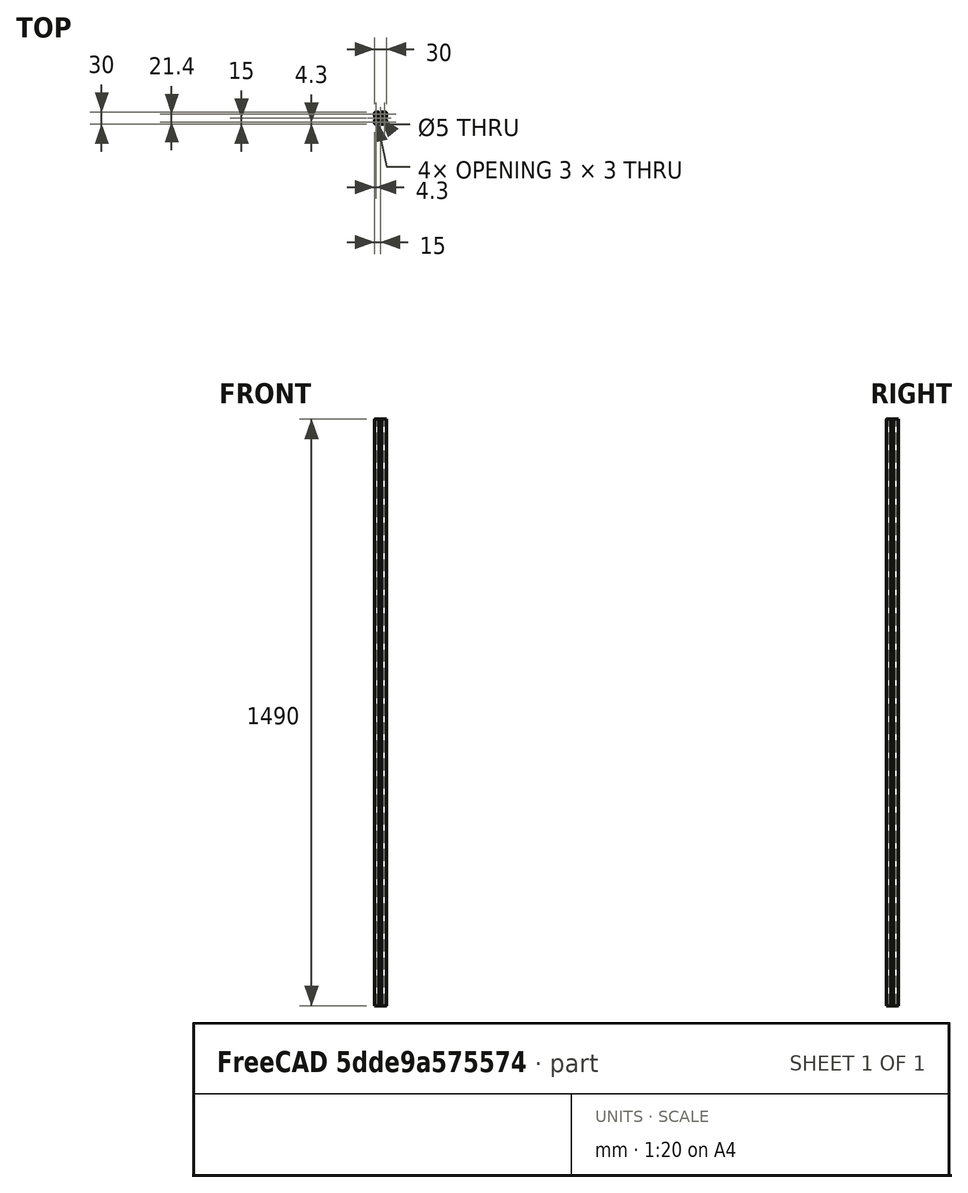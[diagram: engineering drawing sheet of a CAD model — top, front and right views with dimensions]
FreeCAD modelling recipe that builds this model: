
FCSTD DOCUMENT  (FreeCAD 0.19R18353 (Git))
Label: Profile_3030-1490
License: CreativeCommons Attribution
LicenseURL: http://creativecommons.org/licenses/by/4.0/
objects: Sketcher::SketchObject×1, PartDesign::Pad×1, PartDesign::Body×1
note: 4 computed .brp shape members not serialized (recipe doc carries the construction recipe); baked Part::Feature solids carry a one-line shape summary decoded from their .brp

FEATURE [Sketcher::SketchObject] Sketch
  MapMode = 5
  Support = -> [XY_Plane]
  sketch-geometry (137):
    g0: LineSegment [constr] StartX=-5.2 StartY=5.2 StartZ=0 EndX=5.2 EndY=5.2 EndZ=0
    g1: LineSegment [constr] StartX=5.2 StartY=5.2 StartZ=0 EndX=5.2 EndY=-5.2 EndZ=0
    g2: LineSegment [constr] StartX=5.2 StartY=-5.2 StartZ=0 EndX=-5.2 EndY=-5.2 EndZ=0
    g3: LineSegment [constr] StartX=-5.2 StartY=-5.2 StartZ=0 EndX=-5.2 EndY=5.2 EndZ=0
    g4: LineSegment [constr] StartX=-15 StartY=15 StartZ=0 EndX=15 EndY=15 EndZ=0
    g5: LineSegment [constr] StartX=15 StartY=15 StartZ=0 EndX=15 EndY=-15 EndZ=0
    g6: LineSegment [constr] StartX=15 StartY=-15 StartZ=0 EndX=-15 EndY=-15 EndZ=0
    g7: LineSegment [constr] StartX=-15 StartY=-15 StartZ=0 EndX=-15 EndY=15 EndZ=0
    g8: LineSegment [constr] StartX=-12.2 StartY=12.2 StartZ=0 EndX=12.2 EndY=12.2 EndZ=0
    g9: LineSegment [constr] StartX=12.2 StartY=12.2 StartZ=0 EndX=12.2 EndY=-12.2 EndZ=0
    g10: LineSegment [constr] StartX=12.2 StartY=-12.2 StartZ=0 EndX=-12.2 EndY=-12.2 EndZ=0
    g11: LineSegment [constr] StartX=-12.2 StartY=-12.2 StartZ=0 EndX=-12.2 EndY=12.2 EndZ=0
    g12: Circle CenterX=0 CenterY=0 CenterZ=0 NormalX=0 NormalY=0 NormalZ=1 AngleXU=0 Radius=2.5
    g13: LineSegment [constr] StartX=15 StartY=15 StartZ=0 EndX=5.2 EndY=5.2 EndZ=0
    g14: LineSegment [constr] StartX=13.5151 StartY=15 StartZ=0 EndX=15 EndY=13.5151 EndZ=0
    g15: LineSegment [constr] StartX=15 StartY=13.5151 StartZ=0 EndX=5.2 EndY=3.71508 EndZ=0
    g16: LineSegment [constr] StartX=5.2 StartY=3.71508 StartZ=0 EndX=3.71508 EndY=5.2 EndZ=0
    g17: LineSegment [constr] StartX=3.71508 StartY=5.2 StartZ=0 EndX=13.5151 EndY=15 EndZ=0
    g18: LineSegment [constr] StartX=5.2 StartY=-5.2 StartZ=0 EndX=15 EndY=-15 EndZ=0
    g19: LineSegment [constr] StartX=-8.15 StartY=8.15 StartZ=0 EndX=8.15 EndY=8.15 EndZ=0
    g20: LineSegment [constr] StartX=8.15 StartY=8.15 StartZ=0 EndX=8.15 EndY=-8.15 EndZ=0
    g21: LineSegment [constr] StartX=8.15 StartY=-8.15 StartZ=0 EndX=-8.15 EndY=-8.15 EndZ=0
    g22: LineSegment [constr] StartX=-8.15 StartY=-8.15 StartZ=0 EndX=-8.15 EndY=8.15 EndZ=0
    g23: LineSegment [constr] StartX=-15 StartY=3.15 StartZ=0 EndX=15 EndY=3.15 EndZ=0
    g24: LineSegment [constr] StartX=15 StartY=3.15 StartZ=0 EndX=15 EndY=-3.15 EndZ=0
    g25: LineSegment [constr] StartX=15 StartY=-3.15 StartZ=0 EndX=-15 EndY=-3.15 EndZ=0
    g26: LineSegment [constr] StartX=-15 StartY=-3.15 StartZ=0 EndX=-15 EndY=3.15 EndZ=0
    g27: LineSegment [constr] StartX=5.2 StartY=-3.71508 StartZ=0 EndX=3.71508 EndY=-5.2 EndZ=0
    g28: LineSegment [constr] StartX=3.71508 StartY=-5.2 StartZ=0 EndX=13.5151 EndY=-15 EndZ=0
    g29: LineSegment [constr] StartX=13.5151 StartY=-15 StartZ=0 EndX=15 EndY=-13.5151 EndZ=0
    g30: LineSegment [constr] StartX=15 StartY=-13.5151 StartZ=0 EndX=5.2 EndY=-3.71508 EndZ=0
    g31: LineSegment StartX=14 StartY=3.15 StartZ=0 EndX=12.2 EndY=3.15 EndZ=0
    g32: LineSegment StartX=12.2 StartY=3.15 StartZ=0 EndX=12.2 EndY=8.15 EndZ=0
    g33: LineSegment StartX=12.2 StartY=8.15 StartZ=0 EndX=9.63492 EndY=8.15 EndZ=0
    g34: LineSegment StartX=9.63492 StartY=8.15 StartZ=0 EndX=5.2 EndY=3.71508 EndZ=0
    g35: LineSegment StartX=5.2 StartY=3.71508 StartZ=0 EndX=5.2 EndY=-3.71508 EndZ=0
    g36: LineSegment StartX=5.2 StartY=-3.71508 StartZ=0 EndX=9.63492 EndY=-8.15 EndZ=0
    g37: LineSegment StartX=9.63492 StartY=-8.15 StartZ=0 EndX=12.2 EndY=-8.15 EndZ=0
    g38: LineSegment StartX=12.2 StartY=-8.15 StartZ=0 EndX=12.2 EndY=-3.15 EndZ=0
    g39: LineSegment StartX=12.2 StartY=-3.15 StartZ=0 EndX=14 EndY=-3.15 EndZ=0
    g40: LineSegment [constr] StartX=-3.15 StartY=15 StartZ=0 EndX=3.15 EndY=15 EndZ=0
    g41: LineSegment [constr] StartX=3.15 StartY=15 StartZ=0 EndX=3.15 EndY=-15 EndZ=0
    g42: LineSegment [constr] StartX=3.15 StartY=-15 StartZ=0 EndX=-3.15 EndY=-15 EndZ=0
    g43: LineSegment [constr] StartX=-3.15 StartY=-15 StartZ=0 EndX=-3.15 EndY=15 EndZ=0
    g44: LineSegment [constr] StartX=-15 StartY=15 StartZ=0 EndX=-5.2 EndY=5.2 EndZ=0
    g45: LineSegment [constr] StartX=-5.2 StartY=-5.2 StartZ=0 EndX=-15 EndY=-15 EndZ=0
    g46: LineSegment [constr] StartX=-13.5151 StartY=15 StartZ=0 EndX=-15 EndY=13.5151 EndZ=0
    g47: LineSegment [constr] StartX=-15 StartY=13.5151 StartZ=0 EndX=-5.2 EndY=3.71508 EndZ=0
    g48: LineSegment [constr] StartX=-5.2 StartY=3.71508 StartZ=0 EndX=-3.71508 EndY=5.2 EndZ=0
    g49: LineSegment [constr] StartX=-3.71508 StartY=5.2 StartZ=0 EndX=-13.5151 EndY=15 EndZ=0
    g50: LineSegment StartX=15 StartY=4.15 StartZ=0 EndX=15 EndY=13 EndZ=0
    g51: LineSegment StartX=13 StartY=15 StartZ=0 EndX=4.15 EndY=15 EndZ=0
    g52: LineSegment StartX=3.15 StartY=14 StartZ=0 EndX=3.15 EndY=12.2 EndZ=0
    g53: LineSegment StartX=3.15 StartY=12.2 StartZ=0 EndX=8.15 EndY=12.2 EndZ=0
    g54: LineSegment StartX=8.15 StartY=12.2 StartZ=0 EndX=8.15 EndY=9.63492 EndZ=0
    g55: LineSegment StartX=8.15 StartY=9.63492 StartZ=0 EndX=3.71508 EndY=5.2 EndZ=0
    g56: LineSegment StartX=3.71508 StartY=5.2 StartZ=0 EndX=-3.71508 EndY=5.2 EndZ=0
    g57: LineSegment StartX=-3.71508 StartY=5.2 StartZ=0 EndX=-8.15 EndY=9.63492 EndZ=0
    g58: LineSegment StartX=-8.15 StartY=9.63492 StartZ=0 EndX=-8.15 EndY=12.2 EndZ=0
    g59: LineSegment StartX=-8.15 StartY=12.2 StartZ=0 EndX=-3.15 EndY=12.2 EndZ=0
    g60: LineSegment StartX=-3.15 StartY=12.2 StartZ=0 EndX=-3.15 EndY=14 EndZ=0
    g61: LineSegment StartX=-4.15 StartY=15 StartZ=0 EndX=-13 EndY=15 EndZ=0
    g62: ArcOfCircle CenterX=13 CenterY=13 CenterZ=0 NormalX=0 NormalY=0 NormalZ=1 AngleXU=0 Radius=2 StartAngle=0 EndAngle=1.5708
    g63: LineSegment [constr] StartX=-15 StartY=-13.5151 StartZ=0 EndX=-13.5151 EndY=-15 EndZ=0
    g64: LineSegment [constr] StartX=-13.5151 StartY=-15 StartZ=0 EndX=-3.71508 EndY=-5.2 EndZ=0
    g65: LineSegment [constr] StartX=-3.71508 StartY=-5.2 StartZ=0 EndX=-5.2 EndY=-3.71508 EndZ=0
    g66: LineSegment [constr] StartX=-5.2 StartY=-3.71508 StartZ=0 EndX=-15 EndY=-13.5151 EndZ=0
    g67: LineSegment StartX=-15 StartY=13 StartZ=0 EndX=-15 EndY=4.15 EndZ=0
    g68: LineSegment StartX=-14 StartY=3.15 StartZ=0 EndX=-12.2 EndY=3.15 EndZ=0
    g69: LineSegment StartX=-12.2 StartY=3.15 StartZ=0 EndX=-12.2 EndY=8.15 EndZ=0
    g70: LineSegment StartX=-9.63492 StartY=8.15 StartZ=0 EndX=-5.2 EndY=3.71508 EndZ=0
    g71: LineSegment StartX=-5.2 StartY=3.71508 StartZ=0 EndX=-5.2 EndY=-3.71508 EndZ=0
    g72: LineSegment StartX=-5.2 StartY=-3.71508 StartZ=0 EndX=-9.63492 EndY=-8.15 EndZ=0
    g73: LineSegment StartX=-12.2 StartY=-8.15 StartZ=0 EndX=-12.2 EndY=-3.15 EndZ=0
    g74: LineSegment StartX=-12.2 StartY=-3.15 StartZ=0 EndX=-14 EndY=-3.15 EndZ=0
    g75: LineSegment StartX=-15 StartY=-4.15 StartZ=0 EndX=-15 EndY=-13 EndZ=0
    g76: ArcOfCircle CenterX=14 CenterY=4.15 CenterZ=0 NormalX=0 NormalY=0 NormalZ=1 AngleXU=0 Radius=1 StartAngle=4.71239 EndAngle=6.28319
    g77: ArcOfCircle CenterX=4.15 CenterY=14 CenterZ=0 NormalX=0 NormalY=0 NormalZ=1 AngleXU=0 Radius=1 StartAngle=1.5708 EndAngle=3.14159
    g78: ArcOfCircle CenterX=-4.15 CenterY=14 CenterZ=0 NormalX=0 NormalY=0 NormalZ=1 AngleXU=0 Radius=1 StartAngle=0 EndAngle=1.5708
    g79: ArcOfCircle CenterX=-13 CenterY=13 CenterZ=0 NormalX=0 NormalY=0 NormalZ=1 AngleXU=0 Radius=2 StartAngle=1.5708 EndAngle=3.14159
    g80: ArcOfCircle CenterX=-14 CenterY=4.15 CenterZ=0 NormalX=0 NormalY=0 NormalZ=1 AngleXU=0 Radius=1 StartAngle=3.14159 EndAngle=4.71239
    g81: ArcOfCircle CenterX=-14 CenterY=-4.15 CenterZ=0 NormalX=0 NormalY=0 NormalZ=1 AngleXU=0 Radius=1 StartAngle=1.5708 EndAngle=3.14159
    g82: LineSegment StartX=15 StartY=-4.15 StartZ=0 EndX=15 EndY=-13 EndZ=0
    g83: LineSegment StartX=13 StartY=-15 StartZ=0 EndX=4.15 EndY=-15 EndZ=0
    g84: LineSegment StartX=3.15 StartY=-14 StartZ=0 EndX=3.15 EndY=-12.2 EndZ=0
    g85: LineSegment StartX=3.15 StartY=-12.2 StartZ=0 EndX=8.15 EndY=-12.2 EndZ=0
    g86: LineSegment StartX=8.15 StartY=-12.2 StartZ=0 EndX=8.15 EndY=-9.63492 EndZ=0
    g87: LineSegment StartX=8.15 StartY=-9.63492 StartZ=0 EndX=3.71508 EndY=-5.2 EndZ=0
    g88: LineSegment StartX=3.71508 StartY=-5.2 StartZ=0 EndX=-3.71508 EndY=-5.2 EndZ=0
    g89: LineSegment StartX=-3.71508 StartY=-5.2 StartZ=0 EndX=-8.15 EndY=-9.63492 EndZ=0
    g90: LineSegment StartX=-8.15 StartY=-9.63492 StartZ=0 EndX=-8.15 EndY=-12.2 EndZ=0
    g91: LineSegment StartX=-8.15 StartY=-12.2 StartZ=0 EndX=-3.15 EndY=-12.2 EndZ=0
    g92: LineSegment StartX=-3.15 StartY=-12.2 StartZ=0 EndX=-3.15 EndY=-14 EndZ=0
    g93: LineSegment StartX=-4.15 StartY=-15 StartZ=0 EndX=-13 EndY=-15 EndZ=0
    g94: ArcOfCircle CenterX=4.15 CenterY=-14 CenterZ=0 NormalX=0 NormalY=0 NormalZ=1 AngleXU=0 Radius=1 StartAngle=3.14159 EndAngle=4.71239
    g95: ArcOfCircle CenterX=-4.15 CenterY=-14 CenterZ=0 NormalX=0 NormalY=0 NormalZ=1 AngleXU=0 Radius=1 StartAngle=4.71239 EndAngle=6.28319
    g96: ArcOfCircle CenterX=-13 CenterY=-13 CenterZ=0 NormalX=0 NormalY=0 NormalZ=1 AngleXU=0 Radius=2 StartAngle=3.14159 EndAngle=4.71239
    g97: ArcOfCircle CenterX=13 CenterY=-13 CenterZ=0 NormalX=0 NormalY=0 NormalZ=1 AngleXU=0 Radius=2 StartAngle=4.71239 EndAngle=6.28319
    g98: ArcOfCircle CenterX=14 CenterY=-4.15 CenterZ=0 NormalX=0 NormalY=0 NormalZ=1 AngleXU=0 Radius=1 StartAngle=0 EndAngle=1.5708
    g99: LineSegment StartX=-12.2 StartY=8.15 StartZ=0 EndX=-9.63492 EndY=8.15 EndZ=0
    g100: LineSegment StartX=-12.2 StartY=-8.15 StartZ=0 EndX=-9.63492 EndY=-8.15 EndZ=0
    g101: LineSegment [constr] StartX=9.2 StartY=12.2 StartZ=0 EndX=12.2 EndY=12.2 EndZ=0
    g102: LineSegment [constr] StartX=12.2 StartY=12.2 StartZ=0 EndX=12.2 EndY=9.2 EndZ=0
    g103: LineSegment [constr] StartX=12.2 StartY=9.2 StartZ=0 EndX=9.2 EndY=9.2 EndZ=0
    g104: LineSegment [constr] StartX=9.2 StartY=9.2 StartZ=0 EndX=9.2 EndY=12.2 EndZ=0
    g105: LineSegment StartX=9.2 StartY=12.2 StartZ=0 EndX=11.2 EndY=12.2 EndZ=0
    g106: LineSegment StartX=12.2 StartY=9.2 StartZ=0 EndX=9.2 EndY=9.2 EndZ=0
    g107: LineSegment StartX=9.2 StartY=9.2 StartZ=0 EndX=9.2 EndY=12.2 EndZ=0
    g108: ArcOfCircle CenterX=11.2 CenterY=11.2 CenterZ=0 NormalX=0 NormalY=0 NormalZ=1 AngleXU=0 Radius=1 StartAngle=6e-16 EndAngle=1.5708
    g109: LineSegment StartX=12.2 StartY=11.2 StartZ=0 EndX=12.2 EndY=9.2 EndZ=0
    g110: LineSegment [constr] StartX=-12.2 StartY=12.2 StartZ=0 EndX=-9.2 EndY=12.2 EndZ=0
    g111: LineSegment [constr] StartX=-9.2 StartY=12.2 StartZ=0 EndX=-9.2 EndY=9.2 EndZ=0
    g112: LineSegment [constr] StartX=-9.2 StartY=9.2 StartZ=0 EndX=-12.2 EndY=9.2 EndZ=0
    g113: LineSegment [constr] StartX=-12.2 StartY=9.2 StartZ=0 EndX=-12.2 EndY=12.2 EndZ=0
    g114: ArcOfCircle CenterX=-11.2 CenterY=11.2 CenterZ=0 NormalX=0 NormalY=0 NormalZ=1 AngleXU=0 Radius=1 StartAngle=1.5708 EndAngle=3.14159
    g115: LineSegment StartX=-11.2 StartY=12.2 StartZ=0 EndX=-9.2 EndY=12.2 EndZ=0
    g116: LineSegment StartX=-9.2 StartY=12.2 StartZ=0 EndX=-9.2 EndY=9.2 EndZ=0
    g117: LineSegment StartX=-9.2 StartY=9.2 StartZ=0 EndX=-12.2 EndY=9.2 EndZ=0
    g118: LineSegment StartX=-12.2 StartY=9.2 StartZ=0 EndX=-12.2 EndY=11.2 EndZ=0
    g119: LineSegment [constr] StartX=-12.2 StartY=-9.2 StartZ=0 EndX=-9.2 EndY=-9.2 EndZ=0
    g120: LineSegment [constr] StartX=-9.2 StartY=-9.2 StartZ=0 EndX=-9.2 EndY=-12.2 EndZ=0
    g121: LineSegment [constr] StartX=-9.2 StartY=-12.2 StartZ=0 EndX=-12.2 EndY=-12.2 EndZ=0
    g122: LineSegment [constr] StartX=-12.2 StartY=-12.2 StartZ=0 EndX=-12.2 EndY=-9.2 EndZ=0
    g123: ArcOfCircle CenterX=-11.2 CenterY=-11.2 CenterZ=0 NormalX=0 NormalY=0 NormalZ=1 AngleXU=0 Radius=1 StartAngle=3.14159 EndAngle=4.71239
    g124: LineSegment StartX=-12.2 StartY=-11.2 StartZ=0 EndX=-12.2 EndY=-9.2 EndZ=0
    g125: LineSegment StartX=-12.2 StartY=-9.2 StartZ=0 EndX=-9.2 EndY=-9.2 EndZ=0
    g126: LineSegment StartX=-9.2 StartY=-9.2 StartZ=0 EndX=-9.2 EndY=-12.2 EndZ=0
    g127: LineSegment StartX=-9.2 StartY=-12.2 StartZ=0 EndX=-11.2 EndY=-12.2 EndZ=0
    g128: LineSegment [constr] StartX=9.2 StartY=-9.2 StartZ=0 EndX=12.2 EndY=-9.2 EndZ=0
    g129: LineSegment [constr] StartX=12.2 StartY=-9.2 StartZ=0 EndX=12.2 EndY=-12.2 EndZ=0
    g130: LineSegment [constr] StartX=12.2 StartY=-12.2 StartZ=0 EndX=9.2 EndY=-12.2 EndZ=0
    g131: LineSegment [constr] StartX=9.2 StartY=-12.2 StartZ=0 EndX=9.2 EndY=-9.2 EndZ=0
    g132: ArcOfCircle CenterX=11.2 CenterY=-11.2 CenterZ=0 NormalX=0 NormalY=0 NormalZ=1 AngleXU=0 Radius=1 StartAngle=4.71239 EndAngle=6.28319
    g133: LineSegment StartX=12.2 StartY=-11.2 StartZ=0 EndX=12.2 EndY=-9.2 EndZ=0
    g134: LineSegment StartX=12.2 StartY=-9.2 StartZ=0 EndX=9.2 EndY=-9.2 EndZ=0
    g135: LineSegment StartX=9.2 StartY=-9.2 StartZ=0 EndX=9.2 EndY=-12.2 EndZ=0
    g136: LineSegment StartX=9.2 StartY=-12.2 StartZ=0 EndX=11.2 EndY=-12.2 EndZ=0
  constraints (360):
    c: Coincident(g0,g1)
    c: Coincident(g1,g2)
    c: Coincident(g2,g3)
    c: Coincident(g3,g0)
    c: Horizontal(g0)
    c: Horizontal(g2)
    c: Vertical(g1)
    c: Vertical(g3)
    c: Coincident(g4,g5)
    c: Coincident(g5,g6)
    c: Coincident(g6,g7)
    c: Coincident(g7,g4)
    c: Horizontal(g4)
    c: Horizontal(g6)
    c: Vertical(g5)
    c: Vertical(g7)
    c: Coincident(g8,g9)
    c: Coincident(g9,g10)
    c: Coincident(g10,g11)
    c: Coincident(g11,g8)
    c: Horizontal(g8)
    c: Horizontal(g10)
    c: Vertical(g9)
    c: Vertical(g11)
    c: Symmetric(g1,g0,g-1)
    c: Equal(g0,g1)
    c: Symmetric(g8,g9,g-1)
    c: Equal(g8,g9)
    c: Symmetric(g4,g5,g-1)
    c: Equal(g4,g5)
    c: Diameter(g12) = 5
    c: Coincident(g12,g-1)
    c: DistanceY(g1,g1) = 10.4
    c: DistanceY(g5,g5) = 30
    c: DistanceY(g8,g4) = 2.8
    c: Coincident(g13,g4)
    c: Coincident(g13,g0)
    c: Coincident(g14,g15)
    c: Coincident(g15,g16)
    c: Coincident(g16,g17)
    c: Coincident(g17,g14)
    c: Parallel(g17,g13)
    c: Parallel(g13,g15)
    c: Angle(g17,g14) = 1.5708
    c: Angle(g16,g17) = 1.5708
    c: PointOnObject(g15,g1)
    c: PointOnObject(g16,g0)
    c: Distance(g15,g16) = 2.1
    c: PointOnObject(g14,g5)
    c: Coincident(g18,g1)
    c: Coincident(g18,g5)
    c: Coincident(g19,g20)
    c: Coincident(g20,g21)
    c: Coincident(g21,g22)
    c: Coincident(g22,g19)
    c: Horizontal(g19)
    c: Horizontal(g21)
    c: Vertical(g20)
    c: Vertical(g22)
    c: Symmetric(g20,g19,g-1)
    c: Equal(g19,g20)
    c: DistanceY(g20,g20) = 16.3
    c: Coincident(g23,g24)
    c: Coincident(g24,g25)
    c: Coincident(g25,g26)
    c: Coincident(g26,g23)
    c: Horizontal(g23)
    c: Horizontal(g25)
    c: Vertical(g24)
    c: Vertical(g26)
    c: Symmetric(g24,g23,g-1)
    c: DistanceY(g25,g23) = 6.3
    c: PointOnObject(g25,g7)
    c: Coincident(g27,g28)
    c: Coincident(g28,g29)
    c: Coincident(g29,g30)
    c: Coincident(g30,g27)
    c: Equal(g28,g18)
    c: Equal(g18,g30)
    c: PointOnObject(g27,g1)
    c: PointOnObject(g27,g2)
    c: PointOnObject(g28,g6)
    c: PointOnObject(g29,g5)
    c: Angle(g30,g29) = 1.5708
    c: Distance(g29,g28) = 2.1
    c: Horizontal(g31)
    c: Coincident(g31,g32)
    c: Vertical(g32)
    c: Coincident(g32,g33)
    c: Horizontal(g33)
    c: Coincident(g33,g34)
    c: Coincident(g34,g35)
    c: Coincident(g35,g36)
    c: Coincident(g36,g37)
    c: Coincident(g37,g38)
    c: Coincident(g38,g39)
    c: Symmetric(g34,g35,g-1)
    c: Symmetric(g38,g31,g-1)
    c: Symmetric(g37,g32,g-1)
    c: Coincident(g35,g27)
    c: PointOnObject(g32,g9)
    c: PointOnObject(g33,g15)
    c: Symmetric(g36,g33,g-1)
    c: Coincident(g40,g41)
    c: Coincident(g41,g42)
    c: Coincident(g42,g43)
    c: Coincident(g43,g40)
    c: Horizontal(g42)
    c: Vertical(g43)
    c: Symmetric(g41,g40,g-1)
    c: DistanceX(g42,g41) = 6.3
    c: PointOnObject(g41,g6)
    c: Coincident(g44,g4)
    c: Coincident(g44,g0)
    c: Coincident(g45,g2)
    c: Coincident(g45,g6)
    c: Coincident(g46,g47)
    c: Coincident(g47,g48)
    c: Coincident(g48,g49)
    c: Coincident(g49,g46)
    c: Parallel(g49,g47)
    c: Parallel(g47,g44)
    c: Parallel(g46,g48)
    c: Symmetric(g46,g46,g44)
    c: Distance(g46,g46) = 2.1
    c: PointOnObject(g46,g7)
    c: PointOnObject(g47,g3)
    c: Horizontal(g33,g19)
    c: Vertical(g50)
    c: Horizontal(g51)
    c: Coincident(g52,g53)
    c: Horizontal(g53)
    c: Coincident(g53,g54)
    c: Vertical(g54)
    c: Coincident(g54,g55)
    c: Coincident(g55,g56)
    c: Coincident(g56,g57)
    c: Coincident(g57,g58)
    c: Vertical(g58)
    c: Coincident(g58,g59)
    c: Horizontal(g59)
    c: Coincident(g59,g60)
    c: Vertical(g60)
    c: Horizontal(g61)
    c: Symmetric(g55,g56,g-2)
    c: Symmetric(g57,g54,g-2)
    c: Symmetric(g59,g52,g-2)
    c: Vertical(g52)
    c: Coincident(g55,g16)
    c: PointOnObject(g54,g17)
    c: Equal(g37,g54)
    c: PointOnObject(g53,g8)
    c: Tangent(g51,g62) = -1.5708
    c: Tangent(g50,g62) = -1.5708
    c: Radius(g62) = 2
    c: Coincident(g63,g64)
    c: Coincident(g64,g65)
    c: Coincident(g65,g66)
    c: Coincident(g66,g63)
    c: Parallel(g64,g66)
    c: Parallel(g66,g45)
    c: Distance(g63,g63) = 2.1
    c: Parallel(g65,g63)
    c: Symmetric(g64,g65,g45)
    c: PointOnObject(g64,g2)
    c: PointOnObject(g63,g7)
    c: Horizontal(g68)
    c: Coincident(g68,g69)
    c: Vertical(g69)
    c: Coincident(g70,g71)
    c: Coincident(g71,g72)
    c: Vertical(g73)
    c: Coincident(g73,g74)
    c: Horizontal(g74)
    c: Symmetric(g70,g71,g-1)
    c: Coincident(g70,g47)
    c: Tangent(g50,g76) = -1.5708
    c: Tangent(g31,g76) = 1.5708
    c: Radius(g76) = 1
    c: PointOnObject(g50,g5)
    c: Tangent(g51,g77) = -1.5708
    c: Tangent(g52,g77) = -1.5708
    c: Equal(g77,g76)
    c: PointOnObject(g51,g4)
    c: Symmetric(g40,g40,g-2)
    c: PointOnObject(g59,g43)
    c: Tangent(g61,g78) = -1.5708
    c: Tangent(g60,g78) = -1.5708
    c: Equal(g78,g77)
    c: Horizontal(g39)
    c: Tangent(g61,g79) = -1.5708
    c: Tangent(g67,g79) = -1.5708
    c: Equal(g79,g62)
    c: Vertical(g67)
    c: PointOnObject(g61,g4)
    c: Tangent(g67,g80) = -1.5708
    c: Tangent(g68,g80) = -1.5708
    c: Equal(g80,g78)
    c: PointOnObject(g67,g7)
    c: Tangent(g74,g81) = -1.5708
    c: Tangent(g75,g81) = -1.5708
    c: Equal(g80,g81)
    c: PointOnObject(g73,g25)
    c: PointOnObject(g84,g10)
    c: Coincident(g84,g85)
    c: PointOnObject(g85,g10)
    c: Coincident(g85,g86)
    c: PointOnObject(g86,g28)
    c: Vertical(g86)
    c: Coincident(g86,g87)
    c: Coincident(g87,g88)
    c: Coincident(g88,g89)
    c: Coincident(g89,g90)
    c: PointOnObject(g90,g10)
    c: Coincident(g90,g91)
    c: PointOnObject(g91,g10)
    c: Coincident(g91,g92)
    c: Vertical(g92)
    c: Horizontal(g93)
    c: Vertical(g90)
    c: Symmetric(g89,g86,g-2)
    c: Vertical(g84)
    c: PointOnObject(g91,g43)
    c: Symmetric(g88,g87,g-2)
    c: Coincident(g88,g64)
    c: Vertical(g86,g20)
    c: PointOnObject(g68,g23)
    c: Vertical(g75)
    c: Tangent(g84,g94) = 1.5708
    c: Tangent(g83,g94) = 1.5708
    c: Tangent(g92,g95) = 1.5708
    c: Tangent(g93,g95) = 1.5708
    c: Equal(g95,g94)
    c: Equal(g94,g81)
    c: PointOnObject(g84,g41)
    c: Horizontal(g83)
    c: Tangent(g75,g96) = -1.5708
    c: Tangent(g93,g96) = 1.5708
    c: Tangent(g83,g97) = 1.5708
    c: Tangent(g82,g97) = 1.5708
    c: Equal(g79,g96)
    c: Equal(g96,g97)
    c: Vertical(g82)
    c: PointOnObject(g75,g7)
    c: PointOnObject(g93,g6)
    c: PointOnObject(g83,g6)
    c: Tangent(g39,g98) = 1.5708
    c: Tangent(g82,g98) = 1.5708
    c: Equal(g98,g76)
    c: PointOnObject(g38,g25)
    c: PointOnObject(g82,g5)
    c: Horizontal(g99)
    c: Horizontal(g100)
    c: Equal(g99,g58)
    c: Coincident(g69,g99)
    c: Coincident(g70,g99)
    c: PointOnObject(g73,g11)
    c: Equal(g100,g90)
    c: Coincident(g73,g100)
    c: Coincident(g72,g100)
    c: PointOnObject(g72,g66)
    c: Horizontal(g70,g19)
    c: PointOnObject(g70,g47)
    c: Coincident(g101,g102)
    c: Coincident(g102,g103)
    c: Coincident(g103,g104)
    c: Coincident(g104,g101)
    c: Horizontal(g101)
    c: Horizontal(g103)
    c: Vertical(g102)
    c: Vertical(g104)
    c: Equal(g102,g101)
    c: DistanceY(g102,g102) = 3
    c: Coincident(g101,g8)
    c: Coincident(g106,g107)
    c: Coincident(g107,g105)
    c: Horizontal(g105)
    c: Vertical(g107)
    c: Coincident(g106,g103)
    c: PointOnObject(g108,g13)
    c: Horizontal(g108,g108)
    c: Vertical(g108,g108)
    c: Radius(g108) = 1
    c: PointOnObject(g108,g9)
    c: Coincident(g105,g108)
    c: Coincident(g106,g102)
    c: Coincident(g108,g109)
    c: Coincident(g109,g106)
    c: Coincident(g110,g111)
    c: Coincident(g111,g112)
    c: Coincident(g112,g113)
    c: Coincident(g113,g110)
    c: Horizontal(g110)
    c: Horizontal(g112)
    c: Vertical(g111)
    c: Vertical(g113)
    c: Equal(g111,g112)
    c: DistanceY(g111,g111) = 3
    c: Coincident(g110,g8)
    c: PointOnObject(g114,g44)
    c: PointOnObject(g114,g8)
    c: PointOnObject(g114,g11)
    c: Horizontal(g114,g114)
    c: Tangent(g114,g115) = 1.5708
    c: Coincident(g115,g116)
    c: Coincident(g116,g111)
    c: Vertical(g116)
    c: Coincident(g116,g117)
    c: Coincident(g117,g112)
    c: Coincident(g117,g118)
    c: Coincident(g118,g114)
    c: Equal(g108,g114)
    c: Coincident(g119,g120)
    c: Coincident(g120,g121)
    c: Coincident(g121,g122)
    c: Coincident(g122,g119)
    c: Horizontal(g119)
    c: Horizontal(g121)
    c: Vertical(g120)
    c: Vertical(g122)
    c: Equal(g120,g119)
    c: DistanceY(g120,g120) = 3
    c: Coincident(g121,g10)
    c: PointOnObject(g123,g45)
    c: PointOnObject(g123,g10)
    c: PointOnObject(g123,g11)
    c: Vertical(g123,g123)
    c: Tangent(g123,g124) = 1.5708
    c: Coincident(g124,g125)
    c: Coincident(g125,g119)
    c: Horizontal(g125)
    c: Coincident(g125,g126)
    c: Coincident(g126,g120)
    c: Coincident(g126,g127)
    c: Coincident(g127,g123)
    c: Radius(g123) = 1
    c: Coincident(g128,g129)
    c: Coincident(g129,g130)
    c: Coincident(g130,g131)
    c: Coincident(g131,g128)
    c: Horizontal(g128)
    c: Horizontal(g130)
    c: Vertical(g129)
    c: Vertical(g131)
    c: Equal(g128,g131)
    c: DistanceX(g128,g128) = 3
    c: Coincident(g129,g9)
    c: PointOnObject(g132,g18)
    c: PointOnObject(g132,g9)
    c: PointOnObject(g132,g10)
    c: Vertical(g132,g132)
    c: Tangent(g132,g133) = -1.5708
    c: Coincident(g133,g134)
    c: Coincident(g134,g128)
    c: Horizontal(g134)
    c: Coincident(g134,g135)
    c: Coincident(g135,g130)
    c: Coincident(g135,g136)
    c: Coincident(g136,g132)
    c: Radius(g132) = 1
FEATURE [PartDesign::Pad] Pad
  Length = 1490
  Length2 = 100
  Midplane = true
  Profile = -> Sketch
  Refine = true
  Type = 0
FEATURE [PartDesign::Body] Body
  Group = -> [Sketch,Pad]
  Origin = -> Origin
  Tip = -> Pad
